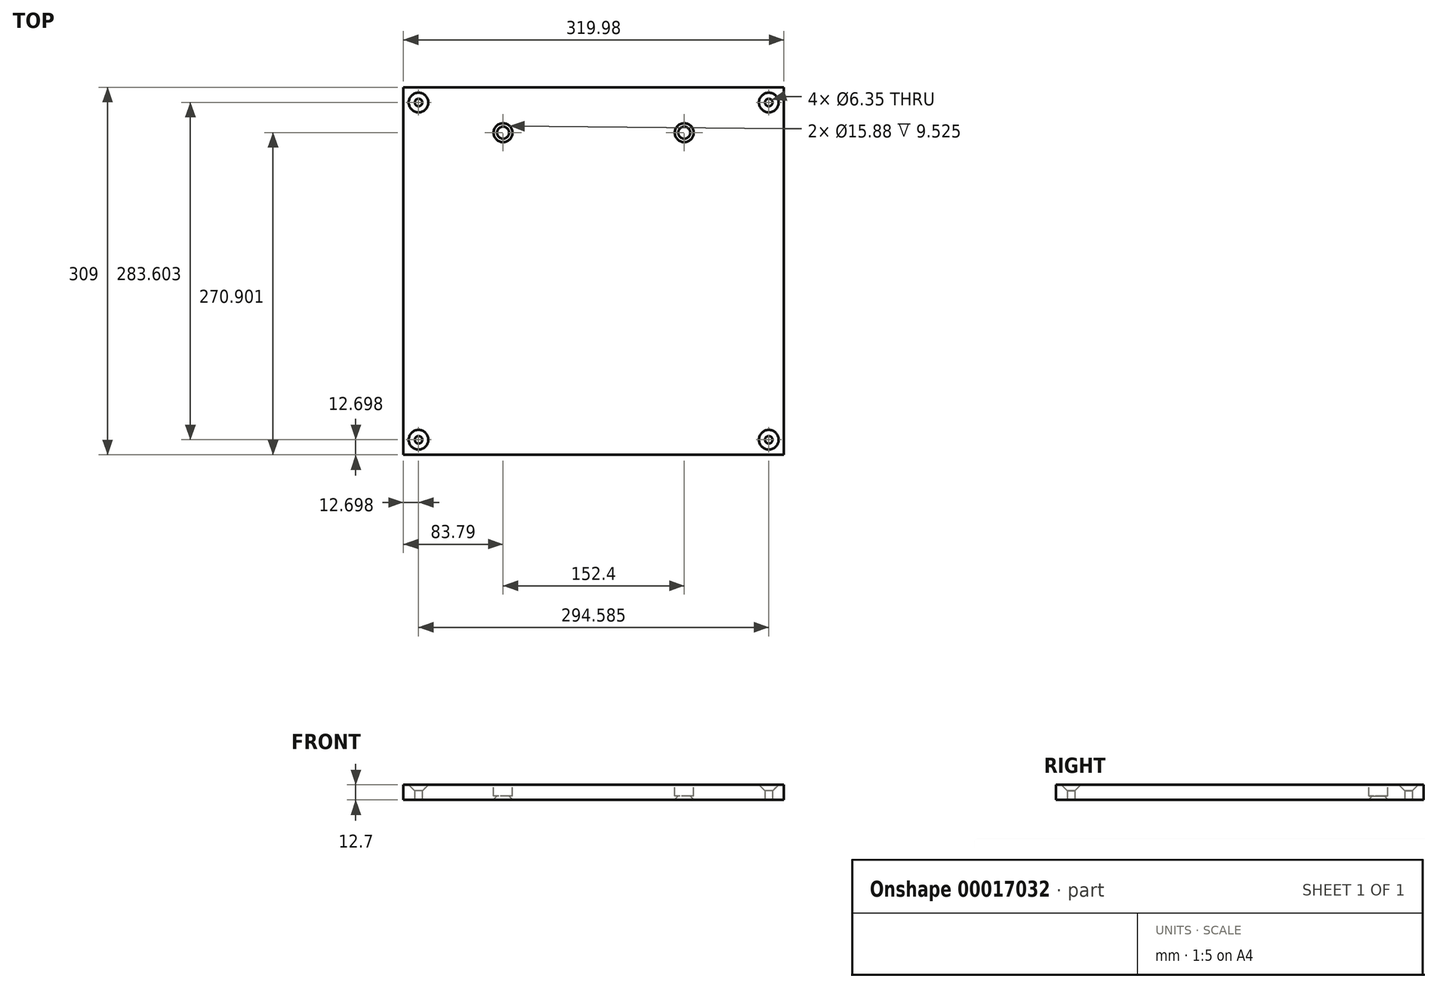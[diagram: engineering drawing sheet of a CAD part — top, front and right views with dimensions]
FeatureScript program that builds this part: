
annotation { "Feature Type Name" : "Feature", "Feature Type Description" : "" }
export const myFeature = defineFeature(function(context is Context, id is Id, definition is map)
    precondition{}
    {
        {
            var Q0;
            Q0=qCreatedBy(makeId("Top.planeOp"),FACE);
            var sketch = newSketch(context, id + "F0", { "sketchPlane" : qUnion([Q0])});
            skLineSegment(sketch, "E0.rect.bottom", {"start": v(160, 154.5) * mm, "end": v(-160, 154.5) * mm});
            skLineSegment(sketch, "E0.rect.top", {"start": v(160, -154.5) * mm, "end": v(-160, -154.5) * mm});
            skLineSegment(sketch, "E0.rect.left", {"start": v(160, 154.5) * mm, "end": v(160, -154.5) * mm});
            skLineSegment(sketch, "E0.rect.right", {"start": v(-160, 154.5) * mm, "end": v(-160, -154.5) * mm});
            skPoint(sketch, "E0.rect.middle", {"position": v(0, 0) * mm});
            skCircle(sketch, "E1", {"center": v(147.3, 141.8) * mm, "radius": 3.18 * mm});
            skCircle(sketch, "E2", {"center": v(147.3, -141.8) * mm, "radius": 3.18 * mm});
            skCircle(sketch, "E3", {"center": v(-147.3, 141.8) * mm, "radius": 3.18 * mm});
            skCircle(sketch, "E4", {"center": v(-147.3, -141.8) * mm, "radius": 3.18 * mm});
            skSolve(sketch);
        }
        {
            var Q0;
            Q0 = qSketchRegion(id + "F0", true);
            extrude(context, id + "F1", {"entities" : qUnion([Q0]), "depth" : 12.7 * mm});
        }
        {
            var Q0;
            Q0=makeQuery(id+"F1.opExtrude","CAP_EDGE",EDGE,{"disambiguationData":[OSD([sQuery(id+"F0.wireOp",EDGE,"E4")])],"isStart":false});
            var Q1;
            Q1=makeQuery(id+"F1.opExtrude","CAP_EDGE",EDGE,{"disambiguationData":[OSD([sQuery(id+"F0.wireOp",EDGE,"E2")])],"isStart":false});
            var Q2;
            Q2=makeQuery(id+"F1.opExtrude","CAP_EDGE",EDGE,{"disambiguationData":[OSD([sQuery(id+"F0.wireOp",EDGE,"E3")])],"isStart":false});
            var Q3;
            Q3=makeQuery(id+"F1.opExtrude","CAP_EDGE",EDGE,{"disambiguationData":[OSD([sQuery(id+"F0.wireOp",EDGE,"E1")])],"isStart":false});
            chamfer(context, id + "F2", {"entities" : qUnion([Q0, Q1, Q2, Q3]), "width" : 5.08 * mm, "tangentPropagation" : true});
        }
        {
            var Q0;
            Q0=makeQuery(id+"F1.opExtrude","CAP_FACE",FACE,{"disambiguationData":[OSD([sQuery(id+"F0.wireOp",EDGE,"E0.rect.bottom"),sQuery(id+"F0.wireOp",EDGE,"E0.rect.top"),sQuery(id+"F0.wireOp",EDGE,"E0.rect.left"),sQuery(id+"F0.wireOp",EDGE,"E0.rect.right"),sQuery(id+"F0.wireOp",EDGE,"E1"),sQuery(id+"F0.wireOp",EDGE,"E2"),sQuery(id+"F0.wireOp",EDGE,"E3"),sQuery(id+"F0.wireOp",EDGE,"E4")])],"isStart":false});
            var sketch = newSketch(context, id + "F3", { "sketchPlane" : qUnion([Q0])});
            skCircle(sketch, "E5", {"center": v(-76.2, 116.4) * mm, "radius": 7.94 * mm});
            skCircle(sketch, "E6", {"center": v(-76.2, 116.4) * mm, "radius": 3.18 * mm});
            skCircle(sketch, "E7", {"center": v(76.2, 116.4) * mm, "radius": 7.94 * mm});
            skCircle(sketch, "E8", {"center": v(76.2, 116.4) * mm, "radius": 3.18 * mm});
            skSolve(sketch);
        }
        {
            var Q0;
            Q0 = qSketchRegion(id + "F3", true);
            extrude(context, id + "F4", {"entities" : qUnion([Q0]), "operationType" : NewBodyOperationType.REMOVE, "oppositeDirection" : true, "depth" : 9.52 * mm});
        }
        {
            var Q0;
            {var subQ0=sQuery(id+"F0.wireOp",EDGE,"E0.rect.bottom");var subQ1=sQuery(id+"F0.wireOp",EDGE,"E0.rect.top");var subQ2=sQuery(id+"F0.wireOp",EDGE,"E0.rect.left");var subQ3=sQuery(id+"F0.wireOp",EDGE,"E0.rect.right");var subQ4=sQuery(id+"F0.wireOp",EDGE,"E1");var subQ5=sQuery(id+"F0.wireOp",EDGE,"E2");var subQ6=sQuery(id+"F0.wireOp",EDGE,"E3");var subQ7=sQuery(id+"F0.wireOp",EDGE,"E4");Q0=makeQuery(id+"F4.boolean.opBoolean","SPLIT",FACE,{"disambiguationData":[TD([makeQuery(id+"F1.opExtrude","SWEPT_FACE",FACE,{"disambiguationData":[OSD([subQ0])]})])],"derivedFrom":makeQuery(id+"F1.opExtrude","CAP_FACE",FACE,{"disambiguationData":[OSD([subQ0,subQ1,subQ2,subQ3,subQ4,subQ5,subQ6,subQ7])],"isStart":false})});}
            var sketch = newSketch(context, id + "F5", { "sketchPlane" : qUnion([Q0])});
            skCircle(sketch, "E9", {"center": v(-76.2, 116.4) * mm, "radius": 3.18 * mm});
            skCircle(sketch, "E10", {"center": v(76.2, 116.4) * mm, "radius": 3.18 * mm});
            skSolve(sketch);
        }
        {
            var Q0;
            Q0 = qSketchRegion(id + "F5", true);
            extrude(context, id + "F6", {"entities" : qUnion([Q0]), "operationType" : NewBodyOperationType.REMOVE, "oppositeDirection" : true, "depth" : 25.4 * mm});
        }
        {
            var Q0;
            Q0=makeQuery(id+"F6.boolean.opBoolean","INTERSECT",EDGE,{"derivedFrom":[makeQuery(id+"F1.opExtrude","CAP_FACE",FACE,{"disambiguationData":[OSD([sQuery(id+"F0.wireOp",EDGE,"E0.rect.bottom"),sQuery(id+"F0.wireOp",EDGE,"E0.rect.top"),sQuery(id+"F0.wireOp",EDGE,"E0.rect.left"),sQuery(id+"F0.wireOp",EDGE,"E0.rect.right"),sQuery(id+"F0.wireOp",EDGE,"E1"),sQuery(id+"F0.wireOp",EDGE,"E2"),sQuery(id+"F0.wireOp",EDGE,"E3"),sQuery(id+"F0.wireOp",EDGE,"E4")])],"isStart":true}),makeQuery(id+"F6.opExtrude","SWEPT_FACE",FACE,{"disambiguationData":[OSD([sQuery(id+"F5.wireOp",EDGE,"E10")])]})]});
            var Q1;
            Q1=makeQuery(id+"F6.boolean.opBoolean","INTERSECT",EDGE,{"derivedFrom":[makeQuery(id+"F1.opExtrude","CAP_FACE",FACE,{"disambiguationData":[OSD([sQuery(id+"F0.wireOp",EDGE,"E0.rect.bottom"),sQuery(id+"F0.wireOp",EDGE,"E0.rect.top"),sQuery(id+"F0.wireOp",EDGE,"E0.rect.left"),sQuery(id+"F0.wireOp",EDGE,"E0.rect.right"),sQuery(id+"F0.wireOp",EDGE,"E1"),sQuery(id+"F0.wireOp",EDGE,"E2"),sQuery(id+"F0.wireOp",EDGE,"E3"),sQuery(id+"F0.wireOp",EDGE,"E4")])],"isStart":true}),makeQuery(id+"F6.opExtrude","SWEPT_FACE",FACE,{"disambiguationData":[OSD([sQuery(id+"F5.wireOp",EDGE,"E9")])]})]});
            chamfer(context, id + "F7", {"entities" : qUnion([Q0, Q1]), "width" : 5.08 * mm, "tangentPropagation" : true});
        }
    });
